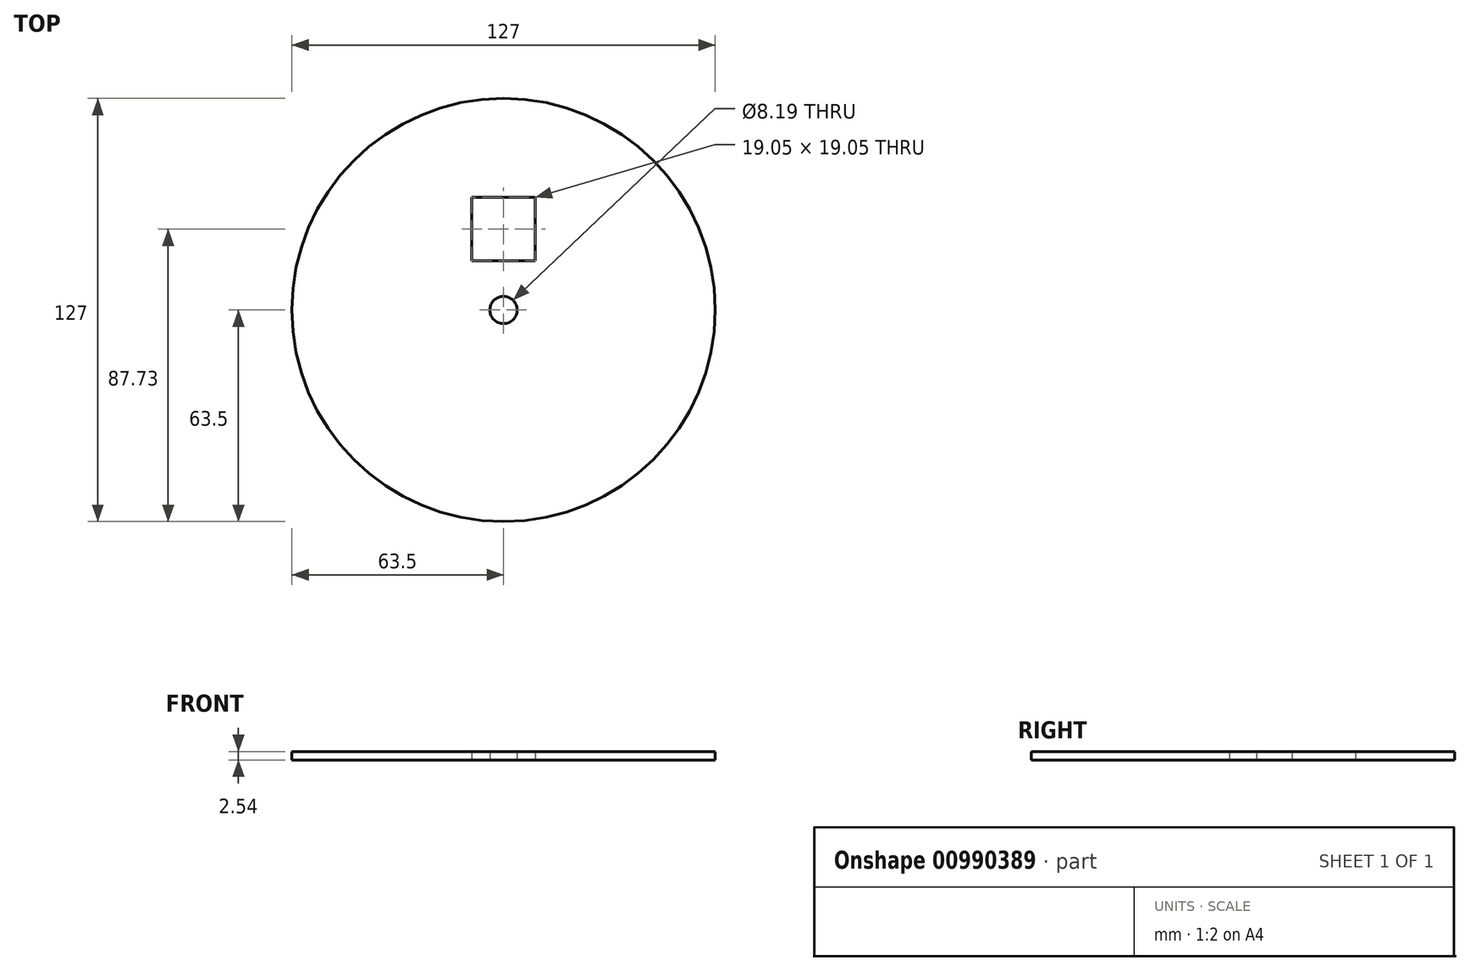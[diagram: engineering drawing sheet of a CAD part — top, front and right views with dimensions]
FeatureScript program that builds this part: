
annotation { "Feature Type Name" : "Feature", "Feature Type Description" : "" }
export const myFeature = defineFeature(function(context is Context, id is Id, definition is map)
    precondition{}
    {
        {
            var Q0;
            Q0=qCreatedBy(makeId("Top.planeOp"),FACE);
            var sketch = newSketch(context, id + "F0", { "sketchPlane" : qUnion([Q0])});
            skCircle(sketch, "E0", {"center": v(0, 0) * mm, "radius": 63.5 * mm});
            skSolve(sketch);
        }
        {
            var Q0;
            Q0=makeQuery(id+"F0.imprint","IMPRINT",FACE,{"disambiguationData":[TD([[makeQuery(id+"F0.imprint","IMPRINT",EDGE,{"derivedFrom":sQuery(id+"F0.wireOp",EDGE,"E0")}),1.0]])]});
            extrude(context, id + "F1", {"entities" : qUnion([Q0]), "depth" : 2.54 * mm, "offsetDistance" : 25.4 * mm});
        }
        {
            var Q0;
            Q0=qCreatedBy(makeId("Top.planeOp"),FACE);
            var sketch = newSketch(context, id + "F2", { "sketchPlane" : qUnion([Q0])});
            skCircle(sketch, "E1", {"center": v(0, 0) * mm, "radius": 4.1 * mm});
            skSolve(sketch);
        }
        {
            var Q0;
            Q0=makeQuery(id+"F2.imprint","IMPRINT",FACE,{"disambiguationData":[TD([[makeQuery(id+"F2.imprint","IMPRINT",EDGE,{"derivedFrom":sQuery(id+"F2.wireOp",EDGE,"E1")}),1.0]])]});
            var Q1;
            Q1=sQuery(id+"F2.wireOp",EDGE,"E1");
            extrude(context, id + "F3", {"entities" : qUnion([Q0]), "operationType" : NewBodyOperationType.REMOVE, "surfaceEntities" : qUnion([Q1]), "oppositeDirection" : true, "depth" : 25.4 * mm, "offsetDistance" : 25.4 * mm});
        }
        {
            var Q0;
            Q0=makeQuery(id+"F2.imprint","IMPRINT",FACE,{"disambiguationData":[TD([[makeQuery(id+"F2.imprint","IMPRINT",EDGE,{"derivedFrom":sQuery(id+"F2.wireOp",EDGE,"E1")}),1.0]])]});
            extrude(context, id + "F4", {"entities" : qUnion([Q0]), "operationType" : NewBodyOperationType.REMOVE, "depth" : 25.4 * mm, "offsetDistance" : 25.4 * mm});
        }
        {
            var Q0;
            Q0=qCreatedBy(makeId("Top.planeOp"),FACE);
            var sketch = newSketch(context, id + "F5", { "sketchPlane" : qUnion([Q0])});
            skLineSegment(sketch, "E2.bottom", {"start": v(-9.52, 14.7) * mm, "end": v(9.53, 14.7) * mm});
            skLineSegment(sketch, "E2.top", {"start": v(-9.52, 33.76) * mm, "end": v(9.53, 33.76) * mm});
            skLineSegment(sketch, "E2.left", {"start": v(-9.52, 14.7) * mm, "end": v(-9.52, 33.76) * mm});
            skLineSegment(sketch, "E2.right", {"start": v(9.53, 14.7) * mm, "end": v(9.53, 33.76) * mm});
            skPoint(sketch, "E2.middle", {"position": v(0, 24.23) * mm});
            skSolve(sketch);
        }
        {
            var Q0;
            Q0=makeQuery(id+"F5.imprint","IMPRINT",FACE,{"disambiguationData":[TD([[makeQuery(id+"F5.imprint","IMPRINT",EDGE,{"derivedFrom":sQuery(id+"F5.wireOp",EDGE,"E2.bottom")}),1.0]])]});
            extrude(context, id + "F6", {"entities" : qUnion([Q0]), "operationType" : NewBodyOperationType.REMOVE, "depth" : 25.4 * mm, "offsetDistance" : 25.4 * mm});
        }
    });
